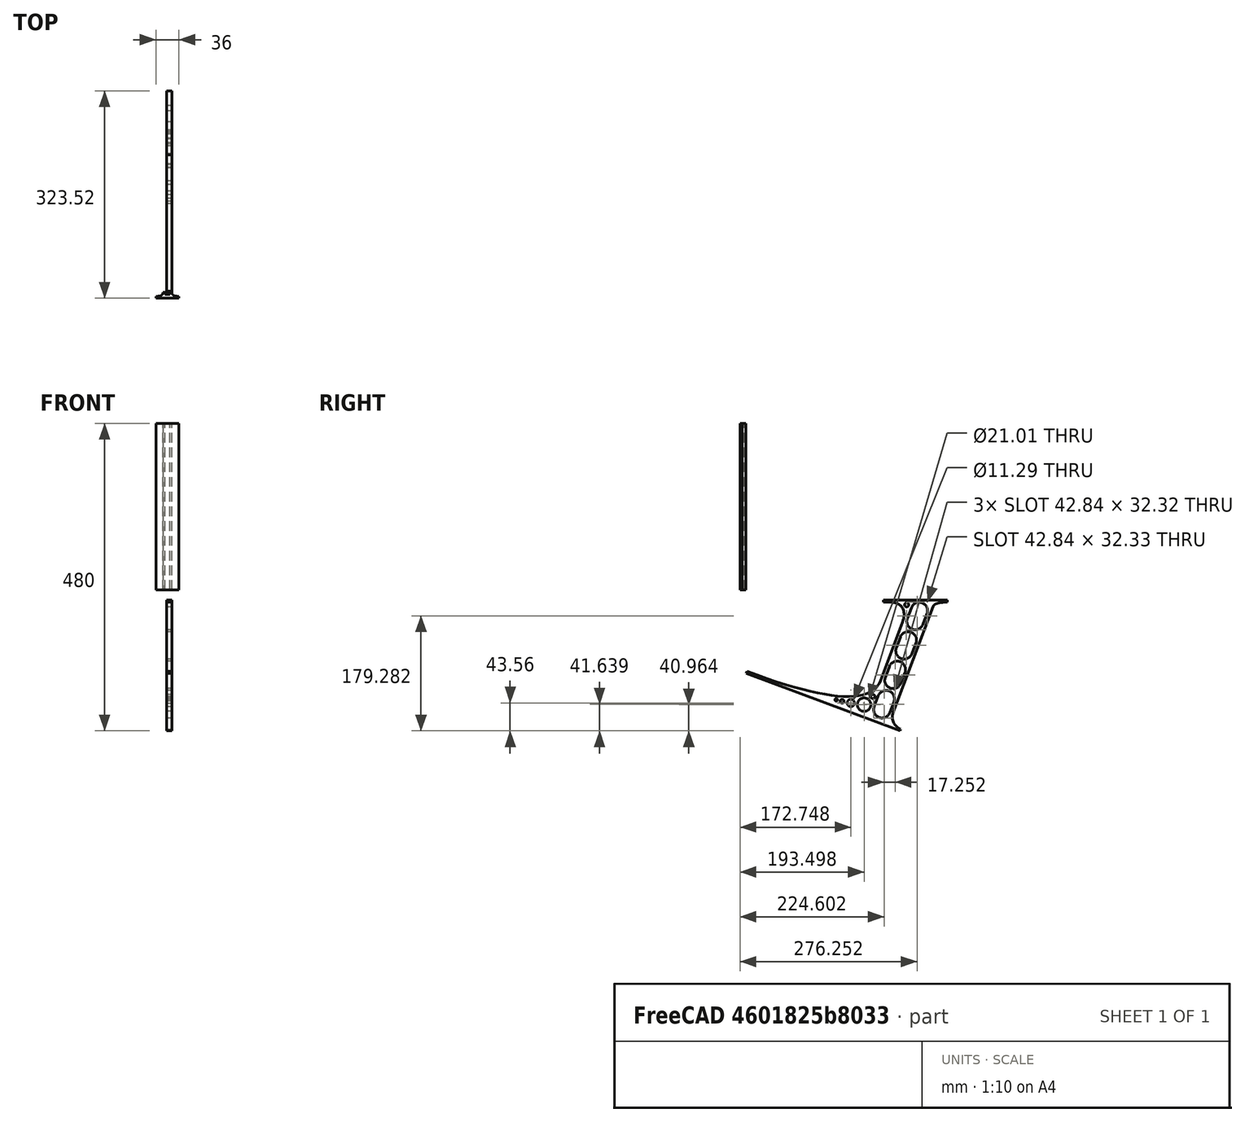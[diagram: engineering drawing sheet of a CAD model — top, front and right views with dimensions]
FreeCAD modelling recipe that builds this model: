
FCSTD DOCUMENT  (FreeCAD 0.19R0.19.2)
Label: laptopStand117FCStd
License: All rights reserved
LicenseURL: http://en.wikipedia.org/wiki/All_rights_reserved
objects: Sketcher::SketchObject×3, Part::Extrusion×3
note: 6 computed .brp shape members not serialized (recipe doc carries the construction recipe); baked Part::Feature solids carry a one-line shape summary decoded from their .brp

FEATURE [Sketcher::SketchObject] Sketch
  FullyConstrained = false
  sketch-geometry (330):
    g0: LineSegment StartX=-10.9272 StartY=-82.7794 StartZ=0 EndX=46.0728 EndY=-51.4823 EndZ=0
    g1: LineSegment StartX=-10.9272 StartY=77.3346 StartZ=0 EndX=-10.9272 EndY=-82.7794 EndZ=0
    g2: LineSegment StartX=-1.92719 StartY=-91.7794 StartZ=0 EndX=46.0728 EndY=-91.7794 EndZ=0
    g3: LineSegment StartX=46.0728 StartY=-65.424 StartZ=0 EndX=-1.92719 EndY=-91.7794 EndZ=0
    g4: LineSegment StartX=46.0728 StartY=-65.424 StartZ=0 EndX=46.0728 EndY=-91.7794 EndZ=0
    g5: LineSegment StartX=46.0728 StartY=77.3346 StartZ=0 EndX=46.0728 EndY=-51.4823 EndZ=0
    g6: LineSegment StartX=-42.9272 StartY=136.221 StartZ=0 EndX=-42.9272 EndY=-103.779 EndZ=0
    g7: LineSegment StartX=407.073 StartY=136.221 StartZ=0 EndX=407.073 EndY=-103.779 EndZ=0
    g8: ArcOfCircle CenterX=-26.9272 CenterY=22.1087 CenterZ=0 NormalX=0 NormalY=0 NormalZ=1 AngleXU=0 Radius=8 StartAngle=1e-16 EndAngle=3.14159
    g9: ArcOfCircle CenterX=-26.9272 CenterY=-83.7794 CenterZ=0 NormalX=0 NormalY=0 NormalZ=1 AngleXU=0 Radius=8 StartAngle=3.14159 EndAngle=6.28319
    g10: LineSegment StartX=-34.9272 StartY=22.1087 StartZ=0 EndX=-34.9272 EndY=-83.7794 EndZ=0
    g11: LineSegment StartX=-18.9272 StartY=22.1087 StartZ=0 EndX=-18.9272 EndY=-83.7794 EndZ=0
    g12: ArcOfCircle CenterX=391.073 CenterY=22.1087 CenterZ=0 NormalX=0 NormalY=0 NormalZ=1 AngleXU=0 Radius=8 StartAngle=-4.4e-15 EndAngle=3.14159
    g13: LineSegment StartX=399.073 StartY=22.1087 StartZ=0 EndX=399.073 EndY=-83.7794 EndZ=0
    g14: LineSegment StartX=383.073 StartY=22.1087 StartZ=0 EndX=383.073 EndY=-83.7794 EndZ=0
    g15: ArcOfCircle CenterX=391.073 CenterY=-83.7794 CenterZ=0 NormalX=0 NormalY=0 NormalZ=1 AngleXU=0 Radius=8 StartAngle=3.14159 EndAngle=6.28319
    g16: Circle CenterX=175.022 CenterY=27.0628 CenterZ=0 NormalX=0 NormalY=0 NormalZ=1 AngleXU=0 Radius=1
    g17: Circle CenterX=179.022 CenterY=24.8665 CenterZ=0 NormalX=0 NormalY=0 NormalZ=1 AngleXU=0 Radius=1
    g18: Circle CenterX=179.022 CenterY=27.0628 CenterZ=0 NormalX=0 NormalY=0 NormalZ=1 AngleXU=0 Radius=1
    g19: BSplineCurve PolesCount=3 KnotsCount=2 Degree=2 IsPeriodic=0
    g20: GeomPoint X=175.022 Y=27.0628 Z=0
    g21: GeomPoint X=179.022 Y=27.0628 Z=0
    g22: Circle CenterX=189.124 CenterY=27.0628 CenterZ=0 NormalX=0 NormalY=0 NormalZ=1 AngleXU=0 Radius=1
    g23: Circle CenterX=185.124 CenterY=24.8665 CenterZ=0 NormalX=0 NormalY=0 NormalZ=1 AngleXU=0 Radius=1
    g24: Circle CenterX=185.124 CenterY=27.0628 CenterZ=0 NormalX=0 NormalY=0 NormalZ=1 AngleXU=0 Radius=1
    g25: BSplineCurve PolesCount=3 KnotsCount=2 Degree=2 IsPeriodic=0
    g26: GeomPoint X=189.124 Y=27.0628 Z=0
    g27: GeomPoint X=185.124 Y=27.0628 Z=0
    g28: Circle CenterX=175.022 CenterY=5.37834 CenterZ=0 NormalX=0 NormalY=0 NormalZ=1 AngleXU=0 Radius=1
    g29: Circle CenterX=179.022 CenterY=7.57463 CenterZ=0 NormalX=0 NormalY=0 NormalZ=1 AngleXU=0 Radius=1
    g30: Circle CenterX=179.022 CenterY=5.34704 CenterZ=0 NormalX=0 NormalY=0 NormalZ=1 AngleXU=0 Radius=1
    g31: BSplineCurve PolesCount=3 KnotsCount=2 Degree=2 IsPeriodic=0
    g32: GeomPoint X=175.022 Y=5.37834 Z=0
    g33: GeomPoint X=179.022 Y=5.34704 Z=0
    g34: Circle CenterX=189.124 CenterY=5.37834 CenterZ=0 NormalX=0 NormalY=0 NormalZ=1 AngleXU=0 Radius=1
    g35: Circle CenterX=185.124 CenterY=7.57463 CenterZ=0 NormalX=0 NormalY=0 NormalZ=1 AngleXU=0 Radius=1
    g36: Circle CenterX=185.124 CenterY=5.34704 CenterZ=0 NormalX=0 NormalY=0 NormalZ=1 AngleXU=0 Radius=1
    g37: BSplineCurve PolesCount=3 KnotsCount=2 Degree=2 IsPeriodic=0
    g38: GeomPoint X=189.124 Y=5.37834 Z=0
    g39: GeomPoint X=185.124 Y=5.34704 Z=0
    g40: Circle CenterX=165.871 CenterY=18.1458 CenterZ=0 NormalX=0 NormalY=0 NormalZ=1 AngleXU=0 Radius=1
    g41: Circle CenterX=169.377 CenterY=16.2206 CenterZ=0 NormalX=0 NormalY=0 NormalZ=1 AngleXU=0 Radius=1
    g42: Circle CenterX=165.871 CenterY=14.2954 CenterZ=0 NormalX=0 NormalY=0 NormalZ=1 AngleXU=0 Radius=1
    g43: BSplineCurve PolesCount=3 KnotsCount=2 Degree=2 IsPeriodic=0
    g44: GeomPoint X=165.871 Y=18.1458 Z=0
    g45: GeomPoint X=165.871 Y=14.2954 Z=0
    g46: Circle CenterX=198.275 CenterY=18.1458 CenterZ=0 NormalX=0 NormalY=0 NormalZ=1 AngleXU=0 Radius=1
    g47: Circle CenterX=194.768 CenterY=16.2206 CenterZ=0 NormalX=0 NormalY=0 NormalZ=1 AngleXU=0 Radius=1
    g48: Circle CenterX=198.275 CenterY=14.2954 CenterZ=0 NormalX=0 NormalY=0 NormalZ=1 AngleXU=0 Radius=1
    g49: BSplineCurve PolesCount=3 KnotsCount=2 Degree=2 IsPeriodic=0
    g50: GeomPoint X=198.275 Y=18.1458 Z=0
    g51: GeomPoint X=198.275 Y=14.2954 Z=0
    g52: LineSegment StartX=407.073 StartY=-103.779 StartZ=0 EndX=-42.9272 EndY=-103.779 EndZ=0
    g53: LineSegment StartX=407.073 StartY=136.221 StartZ=0 EndX=-42.9272 EndY=136.221 EndZ=0
    g54: LineSegment StartX=46.0728 StartY=77.3346 StartZ=0 EndX=-10.9272 EndY=77.3346 EndZ=0
    g55: Circle CenterX=125.607 CenterY=54.1951 CenterZ=0 NormalX=0 NormalY=0 NormalZ=1 AngleXU=0 Radius=1
    g56: Circle CenterX=139.632 CenterY=46.4944 CenterZ=0 NormalX=0 NormalY=0 NormalZ=1 AngleXU=0 Radius=1
    g57: Circle CenterX=127.326 CenterY=56.7187 CenterZ=0 NormalX=0 NormalY=0 NormalZ=1 AngleXU=0 Radius=1
    g58: BSplineCurve PolesCount=3 KnotsCount=2 Degree=2 IsPeriodic=0
    g59: GeomPoint X=125.607 Y=54.1951 Z=0
    g60: GeomPoint X=127.326 Y=56.7187 Z=0
    g61: Circle CenterX=236.821 CenterY=56.7187 CenterZ=0 NormalX=0 NormalY=0 NormalZ=1 AngleXU=0 Radius=1
    g62: Circle CenterX=224.513 CenterY=46.4944 CenterZ=0 NormalX=0 NormalY=0 NormalZ=1 AngleXU=0 Radius=1
    g63: Circle CenterX=238.538 CenterY=54.1951 CenterZ=0 NormalX=0 NormalY=0 NormalZ=1 AngleXU=0 Radius=1
    g64: BSplineCurve PolesCount=3 KnotsCount=2 Degree=2 IsPeriodic=0
    g65: GeomPoint X=236.821 Y=56.7187 Z=0
    g66: GeomPoint X=238.538 Y=54.1951 Z=0
    g67: Circle CenterX=238.538 CenterY=-21.7539 CenterZ=0 NormalX=0 NormalY=0 NormalZ=1 AngleXU=0 Radius=1
    g68: Circle CenterX=224.513 CenterY=-14.0532 CenterZ=0 NormalX=0 NormalY=0 NormalZ=1 AngleXU=0 Radius=1
    g69: Circle CenterX=236.821 CenterY=-24.2775 CenterZ=0 NormalX=0 NormalY=0 NormalZ=1 AngleXU=0 Radius=1
    g70: BSplineCurve PolesCount=3 KnotsCount=2 Degree=2 IsPeriodic=0
    g71: GeomPoint X=238.538 Y=-21.7539 Z=0
    g72: GeomPoint X=236.821 Y=-24.2775 Z=0
    g73: Circle CenterX=125.607 CenterY=-21.7539 CenterZ=0 NormalX=0 NormalY=0 NormalZ=1 AngleXU=0 Radius=1
    g74: Circle CenterX=139.632 CenterY=-14.0532 CenterZ=0 NormalX=0 NormalY=0 NormalZ=1 AngleXU=0 Radius=1
    g75: Circle CenterX=127.325 CenterY=-24.2775 CenterZ=0 NormalX=0 NormalY=0 NormalZ=1 AngleXU=0 Radius=1
    g76: BSplineCurve PolesCount=3 KnotsCount=2 Degree=2 IsPeriodic=0
    g77: GeomPoint X=125.607 Y=-21.7539 Z=0
    g78: GeomPoint X=127.325 Y=-24.2775 Z=0
    g79: Circle CenterX=302.996 CenterY=111.695 CenterZ=0 NormalX=0 NormalY=0 NormalZ=1 AngleXU=0 Radius=1
    g80: Circle CenterX=306.073 CenterY=114.251 CenterZ=0 NormalX=0 NormalY=0 NormalZ=1 AngleXU=0 Radius=1
    g81: Circle CenterX=306.073 CenterY=110.251 CenterZ=0 NormalX=0 NormalY=0 NormalZ=1 AngleXU=0 Radius=1
    g82: BSplineCurve PolesCount=3 KnotsCount=2 Degree=2 IsPeriodic=0
    g83: GeomPoint X=302.996 Y=111.695 Z=0
    g84: GeomPoint X=306.073 Y=110.251 Z=0
    g85: Circle CenterX=306.073 CenterY=95.2763 CenterZ=0 NormalX=0 NormalY=0 NormalZ=1 AngleXU=0 Radius=1
    g86: Circle CenterX=306.073 CenterY=91.2763 CenterZ=0 NormalX=0 NormalY=0 NormalZ=1 AngleXU=0 Radius=1
    g87: Circle CenterX=302.567 CenterY=89.3511 CenterZ=0 NormalX=0 NormalY=0 NormalZ=1 AngleXU=0 Radius=1
    g88: BSplineCurve PolesCount=3 KnotsCount=2 Degree=2 IsPeriodic=0
    g89: GeomPoint X=306.073 Y=95.2763 Z=0
    g90: GeomPoint X=302.567 Y=89.3511 Z=0
    g91: LineSegment StartX=306.073 StartY=110.251 StartZ=0 EndX=306.073 EndY=95.2763 EndZ=0
    g92: LineSegment StartX=302.996 StartY=111.695 StartZ=0 EndX=236.821 EndY=56.7187 EndZ=0
    g93: LineSegment StartX=238.538 StartY=54.1951 StartZ=0 EndX=302.567 EndY=89.3511 EndZ=0
    g94: Circle CenterX=61.1496 CenterY=111.695 CenterZ=0 NormalX=0 NormalY=0 NormalZ=1 AngleXU=0 Radius=1
    g95: Circle CenterX=58.0728 CenterY=114.251 CenterZ=0 NormalX=0 NormalY=0 NormalZ=1 AngleXU=0 Radius=1
    g96: Circle CenterX=58.0728 CenterY=110.251 CenterZ=0 NormalX=0 NormalY=0 NormalZ=1 AngleXU=0 Radius=1
    g97: BSplineCurve PolesCount=3 KnotsCount=2 Degree=2 IsPeriodic=0
    g98: GeomPoint X=61.1496 Y=111.695 Z=0
    g99: GeomPoint X=58.0728 Y=110.251 Z=0
    g100: Circle CenterX=61.5791 CenterY=89.3511 CenterZ=0 NormalX=0 NormalY=0 NormalZ=1 AngleXU=0 Radius=1
    g101: Circle CenterX=58.0728 CenterY=91.2763 CenterZ=0 NormalX=0 NormalY=0 NormalZ=1 AngleXU=0 Radius=1
    g102: Circle CenterX=58.0728 CenterY=95.2763 CenterZ=0 NormalX=0 NormalY=0 NormalZ=1 AngleXU=0 Radius=1
    g103: BSplineCurve PolesCount=3 KnotsCount=2 Degree=2 IsPeriodic=0
    g104: GeomPoint X=61.5791 Y=89.3511 Z=0
    g105: GeomPoint X=58.0728 Y=95.2763 Z=0
    g106: LineSegment StartX=58.0728 StartY=110.251 StartZ=0 EndX=58.0728 EndY=95.2763 EndZ=0
    g107: LineSegment StartX=61.1496 StartY=111.695 StartZ=0 EndX=127.326 EndY=56.7187 EndZ=0
    g108: LineSegment StartX=125.607 StartY=54.1951 StartZ=0 EndX=61.5791 EndY=89.3511 EndZ=0
    g109: Circle CenterX=61.5791 CenterY=-56.9099 CenterZ=0 NormalX=0 NormalY=0 NormalZ=1 AngleXU=0 Radius=1
    g110: Circle CenterX=58.0728 CenterY=-58.8351 CenterZ=0 NormalX=0 NormalY=0 NormalZ=1 AngleXU=0 Radius=1
    g111: Circle CenterX=58.0728 CenterY=-62.8351 CenterZ=0 NormalX=0 NormalY=0 NormalZ=1 AngleXU=0 Radius=1
    g112: BSplineCurve PolesCount=3 KnotsCount=2 Degree=2 IsPeriodic=0
    g113: GeomPoint X=61.5791 Y=-56.9099 Z=0
    g114: GeomPoint X=58.0728 Y=-62.8351 Z=0
    g115: Circle CenterX=58.0728 CenterY=-77.8102 CenterZ=0 NormalX=0 NormalY=0 NormalZ=1 AngleXU=0 Radius=1
    g116: Circle CenterX=58.0728 CenterY=-81.8102 CenterZ=0 NormalX=0 NormalY=0 NormalZ=1 AngleXU=0 Radius=1
    g117: Circle CenterX=61.1496 CenterY=-79.2541 CenterZ=0 NormalX=0 NormalY=0 NormalZ=1 AngleXU=0 Radius=1
    g118: BSplineCurve PolesCount=3 KnotsCount=2 Degree=2 IsPeriodic=0
    g119: GeomPoint X=58.0728 Y=-77.8102 Z=0
    g120: GeomPoint X=61.1496 Y=-79.2541 Z=0
    g121: LineSegment StartX=58.0728 StartY=-62.8351 StartZ=0 EndX=58.0728 EndY=-77.8102 EndZ=0
    g122: LineSegment StartX=61.1496 StartY=-79.2541 StartZ=0 EndX=127.325 EndY=-24.2775 EndZ=0
    g123: LineSegment StartX=125.607 StartY=-21.7539 StartZ=0 EndX=61.5791 EndY=-56.9099 EndZ=0
    g124: Circle CenterX=302.567 CenterY=-56.9099 CenterZ=0 NormalX=0 NormalY=0 NormalZ=1 AngleXU=0 Radius=1
    g125: Circle CenterX=306.073 CenterY=-58.8351 CenterZ=0 NormalX=0 NormalY=0 NormalZ=1 AngleXU=0 Radius=1
    g126: Circle CenterX=306.073 CenterY=-62.8351 CenterZ=0 NormalX=0 NormalY=0 NormalZ=1 AngleXU=0 Radius=1
    g127: BSplineCurve PolesCount=3 KnotsCount=2 Degree=2 IsPeriodic=0
    g128: GeomPoint X=302.567 Y=-56.9099 Z=0
    g129: GeomPoint X=306.073 Y=-62.8351 Z=0
    g130: Circle CenterX=302.996 CenterY=-79.2541 CenterZ=0 NormalX=0 NormalY=0 NormalZ=1 AngleXU=0 Radius=1
    g131: Circle CenterX=306.073 CenterY=-81.8102 CenterZ=0 NormalX=0 NormalY=0 NormalZ=1 AngleXU=0 Radius=1
    g132: Circle CenterX=306.073 CenterY=-77.8102 CenterZ=0 NormalX=0 NormalY=0 NormalZ=1 AngleXU=0 Radius=1
    g133: BSplineCurve PolesCount=3 KnotsCount=2 Degree=2 IsPeriodic=0
    g134: GeomPoint X=302.996 Y=-79.2541 Z=0
    g135: GeomPoint X=306.073 Y=-77.8102 Z=0
    g136: LineSegment StartX=306.073 StartY=-62.8351 StartZ=0 EndX=306.073 EndY=-77.8102 EndZ=0
    g137: LineSegment StartX=302.996 StartY=-79.2541 StartZ=0 EndX=236.821 EndY=-24.2775 EndZ=0
    g138: LineSegment StartX=238.538 StartY=-21.7539 StartZ=0 EndX=302.567 EndY=-56.9099 EndZ=0
    g139: Circle CenterX=61.6457 CenterY=-88.8112 CenterZ=0 NormalX=0 NormalY=0 NormalZ=1 AngleXU=0 Radius=1
    g140: Circle CenterX=58.0728 CenterY=-91.7794 CenterZ=0 NormalX=0 NormalY=0 NormalZ=1 AngleXU=0 Radius=1
    g141: Circle CenterX=63.9135 CenterY=-91.7794 CenterZ=0 NormalX=0 NormalY=0 NormalZ=1 AngleXU=0 Radius=1
    g142: BSplineCurve PolesCount=3 KnotsCount=2 Degree=2 IsPeriodic=0
    g143: GeomPoint X=61.6457 Y=-88.8112 Z=0
    g144: GeomPoint X=63.9135 Y=-91.7794 Z=0
    g145: Circle CenterX=179.022 CenterY=-85.8163 CenterZ=0 NormalX=0 NormalY=0 NormalZ=1 AngleXU=0 Radius=1
    g146: Circle CenterX=179.022 CenterY=-91.7794 CenterZ=0 NormalX=0 NormalY=0 NormalZ=1 AngleXU=0 Radius=1
    g147: Circle CenterX=171.895 CenterY=-91.7794 CenterZ=0 NormalX=0 NormalY=0 NormalZ=1 AngleXU=0 Radius=1
    g148: BSplineCurve PolesCount=3 KnotsCount=2 Degree=2 IsPeriodic=0
    g149: GeomPoint X=179.022 Y=-85.8163 Z=0
    g150: GeomPoint X=171.895 Y=-91.7794 Z=0
    g151: Circle CenterX=185.124 CenterY=-86.2028 CenterZ=0 NormalX=0 NormalY=0 NormalZ=1 AngleXU=0 Radius=1
    g152: Circle CenterX=185.124 CenterY=-91.7794 CenterZ=0 NormalX=0 NormalY=0 NormalZ=1 AngleXU=0 Radius=1
    g153: Circle CenterX=191.747 CenterY=-91.7794 CenterZ=0 NormalX=0 NormalY=0 NormalZ=1 AngleXU=0 Radius=1
    g154: BSplineCurve PolesCount=3 KnotsCount=2 Degree=2 IsPeriodic=0
    g155: GeomPoint X=185.124 Y=-86.2028 Z=0
    g156: GeomPoint X=191.747 Y=-91.7794 Z=0
    g157: Circle CenterX=299.888 CenterY=-86.6413 CenterZ=0 NormalX=0 NormalY=0 NormalZ=1 AngleXU=0 Radius=1
    g158: Circle CenterX=306.073 CenterY=-91.7794 CenterZ=0 NormalX=0 NormalY=0 NormalZ=1 AngleXU=0 Radius=1
    g159: Circle CenterX=298.776 CenterY=-91.7794 CenterZ=0 NormalX=0 NormalY=0 NormalZ=1 AngleXU=0 Radius=1
    g160: BSplineCurve PolesCount=3 KnotsCount=2 Degree=2 IsPeriodic=0
    g161: GeomPoint X=299.888 Y=-86.6413 Z=0
    g162: GeomPoint X=298.776 Y=-91.7794 Z=0
    g163: LineSegment StartX=189.124 StartY=5.37834 StartZ=0 EndX=299.888 EndY=-86.6413 EndZ=0
    g164: LineSegment StartX=298.776 StartY=-91.7794 StartZ=0 EndX=191.747 EndY=-91.7794 EndZ=0
    g165: LineSegment StartX=185.124 StartY=-86.2028 StartZ=0 EndX=185.124 EndY=5.34704 EndZ=0
    g166: LineSegment StartX=179.022 StartY=5.34704 StartZ=0 EndX=179.022 EndY=-85.8163 EndZ=0
    g167: LineSegment StartX=171.895 StartY=-91.7794 StartZ=0 EndX=63.9135 EndY=-91.7794 EndZ=0
    g168: LineSegment StartX=61.6457 StartY=-88.8112 StartZ=0 EndX=175.022 EndY=5.37834 EndZ=0
    g169: Circle CenterX=302.073 CenterY=124.221 CenterZ=0 NormalX=0 NormalY=0 NormalZ=1 AngleXU=0 Radius=1
    g170: Circle CenterX=306.073 CenterY=124.221 CenterZ=0 NormalX=0 NormalY=0 NormalZ=1 AngleXU=0 Radius=1
    g171: Circle CenterX=302.996 CenterY=121.665 CenterZ=0 NormalX=0 NormalY=0 NormalZ=1 AngleXU=0 Radius=1
    g172: BSplineCurve PolesCount=3 KnotsCount=2 Degree=2 IsPeriodic=0
    g173: GeomPoint X=302.073 Y=124.221 Z=0
    g174: GeomPoint X=302.996 Y=121.665 Z=0
    g175: Circle CenterX=189.124 CenterY=124.221 CenterZ=0 NormalX=0 NormalY=0 NormalZ=1 AngleXU=0 Radius=1
    g176: Circle CenterX=185.124 CenterY=124.221 CenterZ=0 NormalX=0 NormalY=0 NormalZ=1 AngleXU=0 Radius=1
    g177: Circle CenterX=185.124 CenterY=120.221 CenterZ=0 NormalX=0 NormalY=0 NormalZ=1 AngleXU=0 Radius=1
    g178: BSplineCurve PolesCount=3 KnotsCount=2 Degree=2 IsPeriodic=0
    g179: GeomPoint X=189.124 Y=124.221 Z=0
    g180: GeomPoint X=185.124 Y=120.221 Z=0
    g181: Circle CenterX=175.022 CenterY=124.221 CenterZ=0 NormalX=0 NormalY=0 NormalZ=1 AngleXU=0 Radius=1
    g182: Circle CenterX=179.022 CenterY=124.221 CenterZ=0 NormalX=0 NormalY=0 NormalZ=1 AngleXU=0 Radius=1
    g183: Circle CenterX=179.022 CenterY=120.221 CenterZ=0 NormalX=0 NormalY=0 NormalZ=1 AngleXU=0 Radius=1
    g184: BSplineCurve PolesCount=3 KnotsCount=2 Degree=2 IsPeriodic=0
    g185: GeomPoint X=175.022 Y=124.221 Z=0
    g186: GeomPoint X=179.022 Y=120.221 Z=0
    g187: Circle CenterX=62.0728 CenterY=124.221 CenterZ=0 NormalX=0 NormalY=0 NormalZ=1 AngleXU=0 Radius=1
    g188: Circle CenterX=58.0728 CenterY=124.221 CenterZ=0 NormalX=0 NormalY=0 NormalZ=1 AngleXU=0 Radius=1
    g189: Circle CenterX=61.1496 CenterY=121.665 CenterZ=0 NormalX=0 NormalY=0 NormalZ=1 AngleXU=0 Radius=1
    g190: BSplineCurve PolesCount=3 KnotsCount=2 Degree=2 IsPeriodic=0
    g191: GeomPoint X=62.0728 Y=124.221 Z=0
    g192: GeomPoint X=61.1496 Y=121.665 Z=0
    g193: LineSegment StartX=62.0728 StartY=124.221 StartZ=0 EndX=175.022 EndY=124.221 EndZ=0
    g194: LineSegment StartX=179.022 StartY=120.221 StartZ=0 EndX=179.022 EndY=27.0628 EndZ=0
    g195: LineSegment StartX=185.124 StartY=27.0628 StartZ=0 EndX=185.124 EndY=120.221 EndZ=0
    g196: LineSegment StartX=189.124 StartY=124.221 StartZ=0 EndX=302.073 EndY=124.221 EndZ=0
    g197: LineSegment StartX=302.996 StartY=121.665 StartZ=0 EndX=189.124 EndY=27.0628 EndZ=0
    g198: LineSegment StartX=175.022 StartY=27.0628 StartZ=0 EndX=61.1496 EndY=121.665 EndZ=0
    g199: Circle CenterX=61.5791 CenterY=75.4095 CenterZ=0 NormalX=0 NormalY=0 NormalZ=1 AngleXU=0 Radius=1
    g200: Circle CenterX=58.0728 CenterY=77.3346 CenterZ=0 NormalX=0 NormalY=0 NormalZ=1 AngleXU=0 Radius=1
    g201: Circle CenterX=58.0728 CenterY=73.3346 CenterZ=0 NormalX=0 NormalY=0 NormalZ=1 AngleXU=0 Radius=1
    g202: BSplineCurve PolesCount=3 KnotsCount=2 Degree=2 IsPeriodic=0
    g203: GeomPoint X=61.5791 Y=75.4095 Z=0
    g204: GeomPoint X=58.0728 Y=73.3346 Z=0
    g205: Circle CenterX=58.0728 CenterY=-40.8935 CenterZ=0 NormalX=0 NormalY=0 NormalZ=1 AngleXU=0 Radius=1
    g206: Circle CenterX=58.0728 CenterY=-44.8935 CenterZ=0 NormalX=0 NormalY=0 NormalZ=1 AngleXU=0 Radius=1
    g207: Circle CenterX=61.5791 CenterY=-42.9683 CenterZ=0 NormalX=0 NormalY=0 NormalZ=1 AngleXU=0 Radius=1
    g208: BSplineCurve PolesCount=3 KnotsCount=2 Degree=2 IsPeriodic=0
    g209: GeomPoint X=58.0728 Y=-40.8935 Z=0
    g210: GeomPoint X=61.5791 Y=-42.9683 Z=0
    g211: LineSegment StartX=61.5791 StartY=-42.9683 StartZ=0 EndX=165.871 EndY=14.2954 EndZ=0
    g212: LineSegment StartX=165.871 StartY=18.1458 StartZ=0 EndX=61.5791 EndY=75.4095 EndZ=0
    g213: LineSegment StartX=58.0728 StartY=73.3346 StartZ=0 EndX=58.0728 EndY=-40.8935 EndZ=0
    g214: Circle CenterX=302.567 CenterY=-42.9683 CenterZ=0 NormalX=0 NormalY=0 NormalZ=1 AngleXU=0 Radius=1
    g215: Circle CenterX=306.073 CenterY=-44.8935 CenterZ=0 NormalX=0 NormalY=0 NormalZ=1 AngleXU=0 Radius=1
    g216: Circle CenterX=306.073 CenterY=-40.8935 CenterZ=0 NormalX=0 NormalY=0 NormalZ=1 AngleXU=0 Radius=1
    g217: BSplineCurve PolesCount=3 KnotsCount=2 Degree=2 IsPeriodic=0
    g218: GeomPoint X=302.567 Y=-42.9683 Z=0
    g219: GeomPoint X=306.073 Y=-40.8935 Z=0
    g220: Circle CenterX=306.073 CenterY=73.3346 CenterZ=0 NormalX=0 NormalY=0 NormalZ=1 AngleXU=0 Radius=1
    g221: Circle CenterX=306.073 CenterY=77.3346 CenterZ=0 NormalX=0 NormalY=0 NormalZ=1 AngleXU=0 Radius=1
    g222: Circle CenterX=302.567 CenterY=75.4095 CenterZ=0 NormalX=0 NormalY=0 NormalZ=1 AngleXU=0 Radius=1
    g223: BSplineCurve PolesCount=3 KnotsCount=2 Degree=2 IsPeriodic=0
    g224: GeomPoint X=306.073 Y=73.3346 Z=0
    g225: GeomPoint X=302.567 Y=75.4095 Z=0
    g226: LineSegment StartX=302.567 StartY=-42.9683 StartZ=0 EndX=198.275 EndY=14.2954 EndZ=0
    g227: LineSegment StartX=198.275 StartY=18.1458 StartZ=0 EndX=302.567 EndY=75.4095 EndZ=0
    g228: LineSegment StartX=306.073 StartY=73.3346 StartZ=0 EndX=306.073 EndY=-40.8935 EndZ=0
    g229: LineSegment StartX=322.073 StartY=105.865 StartZ=0 EndX=328.643 EndY=105.865 EndZ=0
    g230: LineSegment StartX=318.073 StartY=120.221 StartZ=0 EndX=318.073 EndY=109.865 EndZ=0
    g231: LineSegment StartX=336.157 StartY=107.779 StartZ=0 EndX=362.567 EndY=122.294 EndZ=0
    g232: Circle CenterX=362.073 CenterY=124.221 CenterZ=0 NormalX=0 NormalY=0 NormalZ=1 AngleXU=0 Radius=1
    g233: Circle CenterX=366.073 CenterY=124.221 CenterZ=0 NormalX=0 NormalY=0 NormalZ=1 AngleXU=0 Radius=1
    g234: Circle CenterX=362.567 CenterY=122.294 CenterZ=0 NormalX=0 NormalY=0 NormalZ=1 AngleXU=0 Radius=1
    g235: BSplineCurve PolesCount=3 KnotsCount=2 Degree=2 IsPeriodic=0
    g236: GeomPoint X=362.073 Y=124.221 Z=0
    g237: GeomPoint X=362.567 Y=122.294 Z=0
    g238: Circle CenterX=322.073 CenterY=124.221 CenterZ=0 NormalX=0 NormalY=0 NormalZ=1 AngleXU=0 Radius=1
    g239: Circle CenterX=318.073 CenterY=124.221 CenterZ=0 NormalX=0 NormalY=0 NormalZ=1 AngleXU=0 Radius=1
    g240: Circle CenterX=318.073 CenterY=120.221 CenterZ=0 NormalX=0 NormalY=0 NormalZ=1 AngleXU=0 Radius=1
    g241: BSplineCurve PolesCount=3 KnotsCount=2 Degree=2 IsPeriodic=0
    g242: GeomPoint X=322.073 Y=124.221 Z=0
    g243: GeomPoint X=318.073 Y=120.221 Z=0
    g244: Circle CenterX=322.073 CenterY=105.865 CenterZ=0 NormalX=0 NormalY=0 NormalZ=1 AngleXU=0 Radius=1
    g245: Circle CenterX=318.073 CenterY=105.865 CenterZ=0 NormalX=0 NormalY=0 NormalZ=1 AngleXU=0 Radius=1
    g246: Circle CenterX=318.073 CenterY=109.865 CenterZ=0 NormalX=0 NormalY=0 NormalZ=1 AngleXU=0 Radius=1
    g247: BSplineCurve PolesCount=3 KnotsCount=2 Degree=2 IsPeriodic=0
    g248: GeomPoint X=322.073 Y=105.865 Z=0
    g249: GeomPoint X=318.073 Y=109.865 Z=0
    g250: Circle CenterX=336.157 CenterY=107.779 CenterZ=0 NormalX=0 NormalY=0 NormalZ=1 AngleXU=0 Radius=1
    g251: Circle CenterX=332.651 CenterY=105.853 CenterZ=0 NormalX=0 NormalY=0 NormalZ=1 AngleXU=0 Radius=1
    g252: Circle CenterX=328.643 CenterY=105.865 CenterZ=0 NormalX=0 NormalY=0 NormalZ=1 AngleXU=0 Radius=1
    g253: BSplineCurve PolesCount=3 KnotsCount=2 Degree=2 IsPeriodic=0
    g254: GeomPoint X=336.157 Y=107.779 Z=0
    g255: GeomPoint X=328.643 Y=105.865 Z=0
    g256: LineSegment StartX=322.073 StartY=124.221 StartZ=0 EndX=362.073 EndY=124.221 EndZ=0
    g257: Circle CenterX=371.567 CenterY=-80.8644 CenterZ=0 NormalX=0 NormalY=0 NormalZ=1 AngleXU=0 Radius=1
    g258: Circle CenterX=375.073 CenterY=-82.7896 CenterZ=0 NormalX=0 NormalY=0 NormalZ=1 AngleXU=0 Radius=1
    g259: Circle CenterX=375.073 CenterY=-78.7896 CenterZ=0 NormalX=0 NormalY=0 NormalZ=1 AngleXU=0 Radius=1
    g260: BSplineCurve PolesCount=3 KnotsCount=2 Degree=2 IsPeriodic=0
    g261: GeomPoint X=371.567 Y=-80.8644 Z=0
    g262: GeomPoint X=375.073 Y=-78.7896 Z=0
    g263: Circle CenterX=321.579 CenterY=-53.4075 CenterZ=0 NormalX=0 NormalY=0 NormalZ=1 AngleXU=0 Radius=1
    g264: Circle CenterX=318.073 CenterY=-51.4823 CenterZ=0 NormalX=0 NormalY=0 NormalZ=1 AngleXU=0 Radius=1
    g265: Circle CenterX=318.073 CenterY=-47.4823 CenterZ=0 NormalX=0 NormalY=0 NormalZ=1 AngleXU=0 Radius=1
    g266: BSplineCurve PolesCount=3 KnotsCount=2 Degree=2 IsPeriodic=0
    g267: GeomPoint X=321.579 Y=-53.4075 Z=0
    g268: GeomPoint X=318.073 Y=-47.4823 Z=0
    g269: Circle CenterX=318.073 CenterY=79.9235 CenterZ=0 NormalX=0 NormalY=0 NormalZ=1 AngleXU=0 Radius=1
    g270: Circle CenterX=318.073 CenterY=83.9235 CenterZ=0 NormalX=0 NormalY=0 NormalZ=1 AngleXU=0 Radius=1
    g271: Circle CenterX=322.073 CenterY=83.9235 CenterZ=0 NormalX=0 NormalY=0 NormalZ=1 AngleXU=0 Radius=1
    g272: BSplineCurve PolesCount=3 KnotsCount=2 Degree=2 IsPeriodic=0
    g273: GeomPoint X=318.073 Y=79.9235 Z=0
    g274: GeomPoint X=322.073 Y=83.9235 Z=0
    g275: Circle CenterX=375.073 CenterY=79.9235 CenterZ=0 NormalX=0 NormalY=0 NormalZ=1 AngleXU=0 Radius=1
    g276: Circle CenterX=375.073 CenterY=83.9235 CenterZ=0 NormalX=0 NormalY=0 NormalZ=1 AngleXU=0 Radius=1
    g277: Circle CenterX=371.073 CenterY=83.9235 CenterZ=0 NormalX=0 NormalY=0 NormalZ=1 AngleXU=0 Radius=1
    g278: BSplineCurve PolesCount=3 KnotsCount=2 Degree=2 IsPeriodic=0
    g279: GeomPoint X=375.073 Y=79.9235 Z=0
    g280: GeomPoint X=371.073 Y=83.9235 Z=0
    g281: LineSegment StartX=322.073 StartY=83.9235 StartZ=0 EndX=371.073 EndY=83.9235 EndZ=0
    g282: LineSegment StartX=375.073 StartY=79.9235 StartZ=0 EndX=375.073 EndY=-78.7896 EndZ=0
    g283: LineSegment StartX=371.567 StartY=-80.8644 StartZ=0 EndX=321.579 EndY=-53.4075 EndZ=0
    g284: LineSegment StartX=318.073 StartY=-47.4823 StartZ=0 EndX=318.073 EndY=79.9235 EndZ=0
    g285: Circle CenterX=321.579 CenterY=-67.3492 CenterZ=0 NormalX=0 NormalY=0 NormalZ=1 AngleXU=0 Radius=1
    g286: Circle CenterX=318.073 CenterY=-65.424 CenterZ=0 NormalX=0 NormalY=0 NormalZ=1 AngleXU=0 Radius=1
    g287: Circle CenterX=318.073 CenterY=-69.424 CenterZ=0 NormalX=0 NormalY=0 NormalZ=1 AngleXU=0 Radius=1
    g288: BSplineCurve PolesCount=3 KnotsCount=2 Degree=2 IsPeriodic=0
    g289: GeomPoint X=321.579 Y=-67.3492 Z=0
    g290: GeomPoint X=318.073 Y=-69.424 Z=0
    g291: Circle CenterX=362.567 CenterY=-89.8542 CenterZ=0 NormalX=0 NormalY=0 NormalZ=1 AngleXU=0 Radius=1
    g292: Circle CenterX=366.073 CenterY=-91.7794 CenterZ=0 NormalX=0 NormalY=0 NormalZ=1 AngleXU=0 Radius=1
    g293: Circle CenterX=362.073 CenterY=-91.7794 CenterZ=0 NormalX=0 NormalY=0 NormalZ=1 AngleXU=0 Radius=1
    g294: BSplineCurve PolesCount=3 KnotsCount=2 Degree=2 IsPeriodic=0
    g295: GeomPoint X=362.567 Y=-89.8542 Z=0
    g296: GeomPoint X=362.073 Y=-91.7794 Z=0
    g297: Circle CenterX=322.073 CenterY=-91.7794 CenterZ=0 NormalX=0 NormalY=0 NormalZ=1 AngleXU=0 Radius=1
    g298: Circle CenterX=318.073 CenterY=-91.7794 CenterZ=0 NormalX=0 NormalY=0 NormalZ=1 AngleXU=0 Radius=1
    g299: Circle CenterX=318.073 CenterY=-87.7794 CenterZ=0 NormalX=0 NormalY=0 NormalZ=1 AngleXU=0 Radius=1
    g300: BSplineCurve PolesCount=3 KnotsCount=2 Degree=2 IsPeriodic=0
    g301: GeomPoint X=322.073 Y=-91.7794 Z=0
    g302: GeomPoint X=318.073 Y=-87.7794 Z=0
    g303: LineSegment StartX=362.567 StartY=-89.8542 StartZ=0 EndX=321.579 EndY=-67.3492 EndZ=0
    g304: LineSegment StartX=318.073 StartY=-69.424 StartZ=0 EndX=318.073 EndY=-87.7794 EndZ=0
    g305: LineSegment StartX=322.073 StartY=-91.7794 StartZ=0 EndX=362.073 EndY=-91.7794 EndZ=0
    g306: LineSegment StartX=46.0728 StartY=105.865 StartZ=0 EndX=42.0728 EndY=105.865 EndZ=0
    g307: Circle CenterX=2.07281 CenterY=124.221 CenterZ=0 NormalX=0 NormalY=0 NormalZ=1 AngleXU=0 Radius=1
    g308: Circle CenterX=1.57905 CenterY=122.295 CenterZ=0 NormalX=0 NormalY=0 NormalZ=1 AngleXU=0 Radius=1
    g309: BSplineCurve PolesCount=3 KnotsCount=2 Degree=2 IsPeriodic=0
    g310: GeomPoint X=2.07281 Y=124.221 Z=0
    g311: GeomPoint X=1.57905 Y=122.295 Z=0
    g312: Circle CenterX=42.0728 CenterY=124.221 CenterZ=0 NormalX=0 NormalY=0 NormalZ=1 AngleXU=0 Radius=1
    g313: Circle CenterX=46.0728 CenterY=124.221 CenterZ=0 NormalX=0 NormalY=0 NormalZ=1 AngleXU=0 Radius=1
    g314: Circle CenterX=46.0728 CenterY=120.221 CenterZ=0 NormalX=0 NormalY=0 NormalZ=1 AngleXU=0 Radius=1
    g315: BSplineCurve PolesCount=3 KnotsCount=2 Degree=2 IsPeriodic=0
    g316: GeomPoint X=42.0728 Y=124.221 Z=0
    g317: GeomPoint X=46.0728 Y=120.221 Z=0
    g318: Circle CenterX=46.0728 CenterY=109.865 CenterZ=0 NormalX=0 NormalY=0 NormalZ=1 AngleXU=0 Radius=1
    g319: Circle CenterX=46.0728 CenterY=105.865 CenterZ=0 NormalX=0 NormalY=0 NormalZ=1 AngleXU=0 Radius=1
    g320: Circle CenterX=42.0728 CenterY=105.865 CenterZ=0 NormalX=0 NormalY=0 NormalZ=1 AngleXU=0 Radius=1
    g321: BSplineCurve PolesCount=3 KnotsCount=2 Degree=2 IsPeriodic=0
    g322: GeomPoint X=46.0728 Y=109.865 Z=0
    g323: GeomPoint X=42.0728 Y=105.865 Z=0
    g324: Circle CenterX=35.5028 CenterY=105.865 CenterZ=0 NormalX=0 NormalY=0 NormalZ=1 AngleXU=0 Radius=1
    g325: Circle CenterX=31.5028 CenterY=105.865 CenterZ=0 NormalX=0 NormalY=0 NormalZ=1 AngleXU=0 Radius=1
    g326: Circle CenterX=27.9965 CenterY=107.79 CenterZ=0 NormalX=0 NormalY=0 NormalZ=1 AngleXU=0 Radius=1
    g327: BSplineCurve PolesCount=3 KnotsCount=2 Degree=2 IsPeriodic=0
    g328: GeomPoint X=35.5028 Y=105.865 Z=0
    g329: GeomPoint X=27.9965 Y=107.79 Z=0
  constraints (540):
    c: Horizontal(g2)
    c: Coincident(g4,g3)
    c: Coincident(g0,g5)
    c: Block(g4)
    c: Block(g3)
    c: Block(g0)
    c: Block(g1)
    c: Block(g2)
    c: Vertical(g6)
    c: Vertical(g7)
    c: Block(g7)
    c: Block(g6)
    c: Tangent(g8,g11) = 1.5708
    c: Tangent(g8,g10) = -1.5708
    c: Tangent(g10,g9) = -1.5708
    c: Tangent(g11,g9) = 1.5708
    c: Vertical(g10)
    c: Equal(g8,g9)
    c: Block(g11)
    c: Block(g10)
    c: Tangent(g12,g13) = 1.5708
    c: Tangent(g13,g15) = 1.5708
    c: Equal(g12,g15)
    c: Coincident(g14,g12)
    c: Coincident(g14,g15)
    c: Block(g13)
    c: Block(g14)
    c: Weight(g16) = 1
    c: Equal(g16,g17)
    c: Equal(g16,g18)
    c: InternalAlignment(g16,g19)
    c: InternalAlignment(g17,g19)
    c: InternalAlignment(g18,g19)
    c: InternalAlignment(g20,g19)
    c: InternalAlignment(g21,g19)
    c: Weight(g22) = 1
    c: Equal(g22,g23)
    c: Equal(g22,g24)
    c: InternalAlignment(g22,g25)
    c: InternalAlignment(g23,g25)
    c: InternalAlignment(g24,g25)
    c: InternalAlignment(g26,g25)
    c: InternalAlignment(g27,g25)
    c: Block(g25)
    c: Block(g19)
    c: Weight(g28) = 1
    c: Equal(g28,g29)
    c: Equal(g28,g30)
    c: InternalAlignment(g28,g31)
    c: InternalAlignment(g29,g31)
    c: InternalAlignment(g30,g31)
    c: InternalAlignment(g32,g31)
    c: InternalAlignment(g33,g31)
    c: Weight(g34) = 1
    c: Equal(g34,g35)
    c: Equal(g34,g36)
    c: InternalAlignment(g34,g37)
    c: InternalAlignment(g35,g37)
    c: InternalAlignment(g36,g37)
    c: InternalAlignment(g38,g37)
    c: InternalAlignment(g39,g37)
    c: Block(g37)
    c: Block(g31)
    c: Weight(g40) = 1
    c: Equal(g40,g41)
    c: Equal(g40,g42)
    c: InternalAlignment(g40,g43)
    c: InternalAlignment(g41,g43)
    c: InternalAlignment(g42,g43)
    c: InternalAlignment(g44,g43)
    c: InternalAlignment(g45,g43)
    c: Weight(g46) = 1
    c: Equal(g46,g47)
    c: Equal(g46,g48)
    c: InternalAlignment(g46,g49)
    c: InternalAlignment(g47,g49)
    c: InternalAlignment(g48,g49)
    c: InternalAlignment(g50,g49)
    c: InternalAlignment(g51,g49)
    c: Block(g43)
    c: Block(g49)
    c: Coincident(g52,g7)
    c: Coincident(g52,g6)
    c: Horizontal(g52)
    c: Distance(g52) = 450
    c: Coincident(g53,g7)
    c: Coincident(g53,g6)
    c: Horizontal(g53)
    c: Horizontal(g54)
    c: Coincident(g5,g54)
    c: Block(g54)
    c: Coincident(g1,g54)
    c: Weight(g55) = 1
    c: Equal(g55,g56)
    c: Equal(g55,g57)
    c: InternalAlignment(g55,g58)
    c: InternalAlignment(g56,g58)
    c: InternalAlignment(g57,g58)
    c: InternalAlignment(g59,g58)
    c: InternalAlignment(g60,g58)
    c: Block(g58)
    c: Weight(g61) = 1
    c: Equal(g61,g62)
    c: Equal(g61,g63)
    c: InternalAlignment(g61,g64)
    c: InternalAlignment(g62,g64)
    c: InternalAlignment(g63,g64)
    c: InternalAlignment(g65,g64)
    c: InternalAlignment(g66,g64)
    c: Block(g64)
    c: Weight(g67) = 1
    c: Equal(g67,g68)
    c: Equal(g67,g69)
    c: InternalAlignment(g67,g70)
    c: InternalAlignment(g68,g70)
    c: InternalAlignment(g69,g70)
    c: InternalAlignment(g71,g70)
    c: InternalAlignment(g72,g70)
    c: Block(g70)
    c: Weight(g73) = 1
    c: Equal(g73,g74)
    c: Equal(g73,g75)
    c: InternalAlignment(g73,g76)
    c: InternalAlignment(g74,g76)
    c: InternalAlignment(g75,g76)
    c: InternalAlignment(g77,g76)
    c: InternalAlignment(g78,g76)
    c: Block(g76)
    c: Weight(g79) = 1
    c: Equal(g79,g80)
    c: Equal(g79,g81)
    c: InternalAlignment(g79,g82)
    c: InternalAlignment(g80,g82)
    c: InternalAlignment(g81,g82)
    c: InternalAlignment(g83,g82)
    c: InternalAlignment(g84,g82)
    c: Weight(g85) = 1
    c: Equal(g85,g86)
    c: Equal(g85,g87)
    c: InternalAlignment(g85,g88)
    c: InternalAlignment(g86,g88)
    c: InternalAlignment(g87,g88)
    c: InternalAlignment(g89,g88)
    c: InternalAlignment(g90,g88)
    c: Block(g82)
    c: Block(g88)
    c: Coincident(g91,g82)
    c: Coincident(g91,g88)
    c: Vertical(g91)
    c: Coincident(g92,g82)
    c: Coincident(g92,g64)
    c: Coincident(g93,g64)
    c: Coincident(g93,g88)
    c: Weight(g94) = 1
    c: Equal(g94,g95)
    c: Equal(g94,g96)
    c: InternalAlignment(g94,g97)
    c: InternalAlignment(g95,g97)
    c: InternalAlignment(g96,g97)
    c: InternalAlignment(g98,g97)
    c: InternalAlignment(g99,g97)
    c: Weight(g100) = 1
    c: Equal(g100,g101)
    c: Equal(g100,g102)
    c: InternalAlignment(g100,g103)
    c: InternalAlignment(g101,g103)
    c: InternalAlignment(g102,g103)
    c: InternalAlignment(g104,g103)
    c: InternalAlignment(g105,g103)
    c: Block(g97)
    c: Block(g103)
    c: Coincident(g106,g97)
    c: Coincident(g106,g103)
    c: Vertical(g106)
    c: Coincident(g107,g97)
    c: Coincident(g107,g58)
    c: Coincident(g108,g58)
    c: Coincident(g108,g103)
    c: Weight(g109) = 1
    c: Equal(g109,g110)
    c: Equal(g109,g111)
    c: InternalAlignment(g109,g112)
    c: InternalAlignment(g110,g112)
    c: InternalAlignment(g111,g112)
    c: InternalAlignment(g113,g112)
    c: InternalAlignment(g114,g112)
    c: Weight(g115) = 1
    c: Equal(g115,g116)
    c: Equal(g115,g117)
    c: InternalAlignment(g115,g118)
    c: InternalAlignment(g116,g118)
    c: InternalAlignment(g117,g118)
    c: InternalAlignment(g119,g118)
    c: InternalAlignment(g120,g118)
    c: Block(g112)
    c: Block(g118)
    c: Coincident(g121,g112)
    c: Coincident(g121,g118)
    c: Vertical(g121)
    c: Coincident(g122,g118)
    c: Coincident(g122,g76)
    c: Coincident(g123,g76)
    c: Coincident(g123,g112)
    c: Weight(g124) = 1
    c: Equal(g124,g125)
    c: Equal(g124,g126)
    c: InternalAlignment(g124,g127)
    c: InternalAlignment(g125,g127)
    c: InternalAlignment(g126,g127)
    c: InternalAlignment(g128,g127)
    c: InternalAlignment(g129,g127)
    c: Weight(g130) = 1
    c: Equal(g130,g131)
    c: Equal(g130,g132)
    c: InternalAlignment(g130,g133)
    c: InternalAlignment(g131,g133)
    c: InternalAlignment(g132,g133)
    c: InternalAlignment(g134,g133)
    c: InternalAlignment(g135,g133)
    c: Block(g127)
    c: Block(g133)
    c: Coincident(g136,g127)
    c: Coincident(g136,g133)
    c: Vertical(g136)
    c: Coincident(g137,g133)
    c: Coincident(g137,g70)
    c: Coincident(g138,g70)
    c: Coincident(g138,g127)
    c: Weight(g139) = 1
    c: Equal(g139,g140)
    c: Equal(g139,g141)
    c: InternalAlignment(g139,g142)
    c: InternalAlignment(g140,g142)
    c: InternalAlignment(g141,g142)
    c: InternalAlignment(g143,g142)
    c: InternalAlignment(g144,g142)
    c: Weight(g145) = 1
    c: Equal(g145,g146)
    c: Equal(g145,g147)
    c: InternalAlignment(g145,g148)
    c: InternalAlignment(g146,g148)
    c: InternalAlignment(g147,g148)
    c: InternalAlignment(g149,g148)
    c: InternalAlignment(g150,g148)
    c: Weight(g151) = 1
    c: Equal(g151,g152)
    c: Equal(g151,g153)
    c: InternalAlignment(g151,g154)
    c: InternalAlignment(g152,g154)
    c: InternalAlignment(g153,g154)
    c: InternalAlignment(g155,g154)
    c: InternalAlignment(g156,g154)
    c: Weight(g157) = 1
    c: Equal(g157,g158)
    c: Equal(g157,g159)
    c: InternalAlignment(g157,g160)
    c: InternalAlignment(g158,g160)
    c: InternalAlignment(g159,g160)
    c: InternalAlignment(g161,g160)
    c: InternalAlignment(g162,g160)
    c: Block(g160)
    c: Block(g154)
    c: Block(g148)
    c: Block(g142)
    c: Coincident(g163,g37)
    c: Coincident(g163,g160)
    c: Coincident(g164,g160)
    c: Coincident(g164,g154)
    c: Horizontal(g164)
    c: Coincident(g165,g154)
    c: Coincident(g165,g37)
    c: Vertical(g165)
    c: Coincident(g166,g31)
    c: Coincident(g166,g148)
    c: Vertical(g166)
    c: Coincident(g167,g148)
    c: Coincident(g167,g142)
    c: Horizontal(g167)
    c: Coincident(g168,g142)
    c: Coincident(g168,g31)
    c: Weight(g169) = 1
    c: Equal(g169,g170)
    c: Equal(g169,g171)
    c: InternalAlignment(g169,g172)
    c: InternalAlignment(g170,g172)
    c: InternalAlignment(g171,g172)
    c: InternalAlignment(g173,g172)
    c: InternalAlignment(g174,g172)
    c: Weight(g175) = 1
    c: Equal(g175,g176)
    c: Equal(g175,g177)
    c: InternalAlignment(g175,g178)
    c: InternalAlignment(g176,g178)
    c: InternalAlignment(g177,g178)
    c: InternalAlignment(g179,g178)
    c: InternalAlignment(g180,g178)
    c: Weight(g181) = 1
    c: Equal(g181,g182)
    c: Equal(g181,g183)
    c: InternalAlignment(g181,g184)
    c: InternalAlignment(g182,g184)
    c: InternalAlignment(g183,g184)
    c: InternalAlignment(g185,g184)
    c: InternalAlignment(g186,g184)
    c: Weight(g187) = 1
    c: Equal(g187,g188)
    c: Equal(g187,g189)
    c: InternalAlignment(g187,g190)
    c: InternalAlignment(g188,g190)
    c: InternalAlignment(g189,g190)
    c: InternalAlignment(g191,g190)
    c: InternalAlignment(g192,g190)
    c: Block(g190)
    c: Block(g184)
    c: Block(g178)
    c: Block(g172)
    c: Coincident(g193,g190)
    c: Coincident(g193,g184)
    c: Horizontal(g193)
    c: Coincident(g194,g184)
    c: Coincident(g194,g19)
    c: Vertical(g194)
    c: Coincident(g195,g25)
    c: Coincident(g195,g178)
    c: Vertical(g195)
    c: Coincident(g196,g178)
    c: Coincident(g196,g172)
    c: Horizontal(g196)
    c: Coincident(g197,g172)
    c: Coincident(g197,g25)
    c: Coincident(g198,g19)
    c: Weight(g199) = 1
    c: Equal(g199,g200)
    c: Equal(g199,g201)
    c: InternalAlignment(g199,g202)
    c: InternalAlignment(g200,g202)
    c: InternalAlignment(g201,g202)
    c: InternalAlignment(g203,g202)
    c: InternalAlignment(g204,g202)
    c: Weight(g205) = 1
    c: Equal(g205,g206)
    c: Equal(g205,g207)
    c: InternalAlignment(g205,g208)
    c: InternalAlignment(g206,g208)
    c: InternalAlignment(g207,g208)
    c: InternalAlignment(g209,g208)
    c: InternalAlignment(g210,g208)
    c: Block(g208)
    c: Block(g202)
    c: Coincident(g211,g208)
    c: Coincident(g211,g43)
    c: Coincident(g212,g43)
    c: Coincident(g212,g202)
    c: Coincident(g213,g202)
    c: Coincident(g213,g208)
    c: Vertical(g213)
    c: Weight(g214) = 1
    c: Equal(g214,g215)
    c: Equal(g214,g216)
    c: InternalAlignment(g214,g217)
    c: InternalAlignment(g215,g217)
    c: InternalAlignment(g216,g217)
    c: InternalAlignment(g218,g217)
    c: InternalAlignment(g219,g217)
    c: Weight(g220) = 1
    c: Equal(g220,g221)
    c: Equal(g220,g222)
    c: InternalAlignment(g220,g223)
    c: InternalAlignment(g221,g223)
    c: InternalAlignment(g222,g223)
    c: InternalAlignment(g224,g223)
    c: InternalAlignment(g225,g223)
    c: Block(g223)
    c: Block(g217)
    c: Coincident(g226,g217)
    c: Coincident(g226,g49)
    c: Coincident(g227,g49)
    c: Coincident(g227,g223)
    c: Coincident(g228,g223)
    c: Coincident(g228,g217)
    c: Vertical(g228)
    c: Horizontal(g229)
    c: Block(g229)
    c: Vertical(g230)
    c: Block(g230)
    c: Block(g231)
    c: Weight(g232) = 1
    c: Equal(g232,g233)
    c: Equal(g232,g234)
    c: InternalAlignment(g232,g235)
    c: InternalAlignment(g233,g235)
    c: InternalAlignment(g234,g235)
    c: InternalAlignment(g236,g235)
    c: InternalAlignment(g237,g235)
    c: Weight(g238) = 1
    c: Equal(g238,g239)
    c: Equal(g238,g240)
    c: InternalAlignment(g238,g241)
    c: InternalAlignment(g239,g241)
    c: InternalAlignment(g240,g241)
    c: InternalAlignment(g242,g241)
    c: InternalAlignment(g243,g241)
    c: Weight(g244) = 1
    c: Equal(g244,g245)
    c: Equal(g244,g246)
    c: InternalAlignment(g244,g247)
    c: InternalAlignment(g245,g247)
    c: InternalAlignment(g246,g247)
    c: InternalAlignment(g248,g247)
    c: InternalAlignment(g249,g247)
    c: Weight(g250) = 1
    c: Equal(g250,g251)
    c: Equal(g250,g252)
    c: InternalAlignment(g250,g253)
    c: InternalAlignment(g251,g253)
    c: InternalAlignment(g252,g253)
    c: InternalAlignment(g254,g253)
    c: InternalAlignment(g255,g253)
    c: Block(g235)
    c: Block(g241)
    c: Block(g247)
    c: Block(g253)
    c: Coincident(g256,g241)
    c: Coincident(g256,g235)
    c: Horizontal(g256)
    c: Block(g198)
    c: Weight(g257) = 1
    c: Equal(g257,g258)
    c: Equal(g257,g259)
    c: InternalAlignment(g257,g260)
    c: InternalAlignment(g258,g260)
    c: InternalAlignment(g259,g260)
    c: InternalAlignment(g261,g260)
    c: InternalAlignment(g262,g260)
    c: Weight(g263) = 1
    c: Equal(g263,g264)
    c: Equal(g263,g265)
    c: InternalAlignment(g263,g266)
    c: InternalAlignment(g264,g266)
    c: InternalAlignment(g265,g266)
    c: InternalAlignment(g267,g266)
    c: InternalAlignment(g268,g266)
    c: Weight(g269) = 1
    c: Equal(g269,g270)
    c: Equal(g269,g271)
    c: InternalAlignment(g269,g272)
    c: InternalAlignment(g270,g272)
    c: InternalAlignment(g271,g272)
    c: InternalAlignment(g273,g272)
    c: InternalAlignment(g274,g272)
    c: Weight(g275) = 1
    c: Equal(g275,g276)
    c: Equal(g275,g277)
    c: InternalAlignment(g275,g278)
    c: InternalAlignment(g276,g278)
    c: InternalAlignment(g277,g278)
    c: InternalAlignment(g279,g278)
    c: InternalAlignment(g280,g278)
    c: Block(g260)
    c: Block(g266)
    c: Block(g272)
    c: Block(g278)
    c: Coincident(g281,g272)
    c: Coincident(g281,g278)
    c: Horizontal(g281)
    c: Coincident(g282,g278)
    c: Coincident(g282,g260)
    c: Vertical(g282)
    c: Coincident(g283,g260)
    c: Coincident(g283,g266)
    c: Coincident(g284,g266)
    c: Coincident(g284,g272)
    c: Vertical(g284)
    c: Weight(g285) = 1
    c: Equal(g285,g286)
    c: Equal(g285,g287)
    c: InternalAlignment(g285,g288)
    c: InternalAlignment(g286,g288)
    c: InternalAlignment(g287,g288)
    c: InternalAlignment(g289,g288)
    c: InternalAlignment(g290,g288)
    c: Weight(g291) = 1
    c: Equal(g291,g292)
    c: Equal(g291,g293)
    c: InternalAlignment(g291,g294)
    c: InternalAlignment(g292,g294)
    c: InternalAlignment(g293,g294)
    c: InternalAlignment(g295,g294)
    c: InternalAlignment(g296,g294)
    c: Weight(g297) = 1
    c: Equal(g297,g298)
    c: Equal(g297,g299)
    c: InternalAlignment(g297,g300)
    c: InternalAlignment(g298,g300)
    c: InternalAlignment(g299,g300)
    c: InternalAlignment(g301,g300)
    c: InternalAlignment(g302,g300)
    c: Block(g300)
    c: Block(g294)
    c: Block(g288)
    c: Coincident(g303,g294)
    c: Coincident(g303,g288)
    c: Coincident(g304,g288)
    c: Coincident(g304,g300)
    c: Vertical(g304)
    c: Coincident(g305,g300)
    c: Coincident(g305,g294)
    c: Horizontal(g305)
    c: Horizontal(g306)
    c: Distance(g306) = 4
    c: Weight(g307) = 1
    c: Equal(g307,g308)
    c: InternalAlignment(g307,g309)
    c: InternalAlignment(g308,g309)
    c: InternalAlignment(g310,g309)
    c: InternalAlignment(g311,g309)
    c: Weight(g312) = 1
    c: Equal(g312,g313)
    c: Equal(g312,g314)
    c: InternalAlignment(g312,g315)
    c: InternalAlignment(g313,g315)
    c: InternalAlignment(g314,g315)
    c: InternalAlignment(g316,g315)
    c: InternalAlignment(g317,g315)
    c: Weight(g318) = 1
    c: Equal(g318,g319)
    c: Equal(g318,g320)
    c: Coincident(g321,g306)
    c: InternalAlignment(g318,g321)
    c: InternalAlignment(g319,g321)
    c: InternalAlignment(g320,g321)
    c: InternalAlignment(g322,g321)
    c: InternalAlignment(g323,g321)
    c: Equal(g324,g325)
    c: Equal(g324,g326)
    c: InternalAlignment(g324,g327)
    c: InternalAlignment(g325,g327)
    c: InternalAlignment(g326,g327)
    c: InternalAlignment(g328,g327)
    c: InternalAlignment(g329,g327)
FEATURE [Sketcher::SketchObject] Sketch001
  FullyConstrained = true
  MapMode = 4
  Placement = pos=(0,0,0) rot=(0.57735,0.57735,0.57735;2.0944rad)
  Support = -> [Sketch]
  sketch-geometry (46):
    g0: BSplineCurve PolesCount=3 KnotsCount=2 Degree=2 IsPeriodic=0
    g1: ArcOfCircle CenterX=73.1223 CenterY=-32.291 CenterZ=0 NormalX=0 NormalY=0 NormalZ=1 AngleXU=0 Radius=13 StartAngle=5.92268 EndAngle=9.06428
    g2: ArcOfCircle CenterX=66.7816 CenterY=-49.1439 CenterZ=0 NormalX=0 NormalY=0 NormalZ=1 AngleXU=0 Radius=13 StartAngle=2.78068 EndAngle=5.92131
    g3: ArcOfCircle CenterX=55.9263 CenterY=-78.1807 CenterZ=0 NormalX=0 NormalY=0 NormalZ=1 AngleXU=0 Radius=13 StartAngle=5.92268 EndAngle=9.06428
    g4: ArcOfCircle CenterX=49.5884 CenterY=-95.0342 CenterZ=0 NormalX=0 NormalY=0 NormalZ=1 AngleXU=0 Radius=13 StartAngle=2.78068 EndAngle=5.92131
    g5: ArcOfCircle CenterX=38.7206 CenterY=-124.067 CenterZ=0 NormalX=0 NormalY=0 NormalZ=1 AngleXU=0 Radius=13 StartAngle=5.92268 EndAngle=9.06428
    g6: ArcOfCircle CenterX=32.3875 CenterY=-140.92 CenterZ=0 NormalX=0 NormalY=0 NormalZ=1 AngleXU=0 Radius=13 StartAngle=2.78068 EndAngle=5.92131
    g7: ArcOfCircle CenterX=21.4715 CenterY=-169.934 CenterZ=0 NormalX=0 NormalY=0 NormalZ=1 AngleXU=0 Radius=13 StartAngle=5.92268 EndAngle=9.06428
    g8: ArcOfCircle CenterX=15.1336 CenterY=-186.787 CenterZ=0 NormalX=0 NormalY=0 NormalZ=1 AngleXU=0 Radius=13 StartAngle=2.78068 EndAngle=5.92131
    g9-g12: Circle x4 (B-spline internal-alignment scaffolding for g13; pole/knot coordinates omitted)
    g13: BSplineCurve PolesCount=4 KnotsCount=2 Degree=3 IsPeriodic=0
    g14: GeomPoint X=28.8094 Y=-19.0875 Z=0
    g15: GeomPoint X=47.0443 Y=-50.4712 Z=0
    g16: Circle CenterX=53.5586 CenterY=-23.2695 CenterZ=0 NormalX=0 NormalY=0 NormalZ=1 AngleXU=0 Radius=3.24518
    g17: Circle CenterX=-195.441 CenterY=-127.082 CenterZ=0 NormalX=0 NormalY=0 NormalZ=1 AngleXU=0 Radius=1
    g18: Circle CenterX=-8.24091 CenterY=-197.481 CenterZ=0 NormalX=0 NormalY=0 NormalZ=1 AngleXU=0 Radius=1
    g19: Circle CenterX=12.8789 CenterY=-141.321 CenterZ=0 NormalX=0 NormalY=0 NormalZ=1 AngleXU=0 Radius=1
    g20: BSplineCurve PolesCount=3 KnotsCount=2 Degree=2 IsPeriodic=0
    g21: GeomPoint X=-195.441 Y=-127.082 Z=0
    g22: GeomPoint X=12.8789 Y=-141.321 Z=0
    g23: Circle CenterX=-12.8016 CenterY=-179.036 CenterZ=0 NormalX=0 NormalY=0 NormalZ=1 AngleXU=0 Radius=10.5072
    g24: Circle CenterX=0.933922 CenterY=-166.43 CenterZ=0 NormalX=0 NormalY=0 NormalZ=1 AngleXU=0 Radius=3.26661
    g25: Circle CenterX=-33.5518 CenterY=-176.44 CenterZ=0 NormalX=0 NormalY=0 NormalZ=1 AngleXU=0 Radius=5.64388
    g26: Circle CenterX=-47.2366 CenterY=-173.859 CenterZ=0 NormalX=0 NormalY=0 NormalZ=1 AngleXU=0 Radius=3.01653
    g27: Circle CenterX=-56.2595 CenterY=-171.456 CenterZ=0 NormalX=0 NormalY=0 NormalZ=1 AngleXU=0 Radius=2.12826
    g28: ArcOfCircle CenterX=51.2151 CenterY=-198.473 CenterZ=0 NormalX=0 NormalY=0 NormalZ=1 AngleXU=0 Radius=20 StartAngle=2.78189 EndAngle=4.35269
    g29: LineSegment StartX=32.4951 StartY=-191.433 StartZ=0 EndX=94.6578 EndY=-26.1352 EndZ=0
    g30: LineSegment StartX=43.1192 StartY=-220.001 StartZ=0 EndX=-196.497 EndY=-129.89 EndZ=0
    g31: LineSegment StartX=43.1192 StartY=-220.001 StartZ=0 EndX=44.1752 EndY=-217.193 EndZ=0
    g32: LineSegment StartX=117.223 StartY=-19.0875 StartZ=0 EndX=117.223 EndY=-16.0875 EndZ=0
    g33: LineSegment StartX=117.223 StartY=-16.0875 StartZ=0 EndX=17.2232 EndY=-16.0875 EndZ=0
    g34: LineSegment StartX=17.2232 StartY=-16.0875 StartZ=0 EndX=17.2232 EndY=-19.0875 EndZ=0
    g35: LineSegment StartX=28.8094 StartY=-19.0875 StartZ=0 EndX=17.2232 EndY=-19.0875 EndZ=0
    g36: LineSegment StartX=47.0443 StartY=-50.4712 StartZ=0 EndX=12.8789 EndY=-141.321 EndZ=0
    g37: LineSegment StartX=-195.441 StartY=-127.082 StartZ=0 EndX=-196.497 EndY=-129.89 EndZ=0
    g38: LineSegment StartX=85.2866 StartY=-36.8766 StartZ=0 EndX=78.9396 EndY=-53.7463 EndZ=0
    g39: LineSegment StartX=60.9579 StartY=-27.7053 StartZ=0 EndX=54.6191 EndY=-44.5532 EndZ=0
    g40: LineSegment StartX=68.0907 StartY=-82.7664 StartZ=0 EndX=61.7465 EndY=-99.6365 EndZ=0
    g41: LineSegment StartX=43.7619 StartY=-73.595 StartZ=0 EndX=37.426 EndY=-90.4435 EndZ=0
    g42: LineSegment StartX=50.885 StartY=-128.652 StartZ=0 EndX=44.5456 EndY=-145.522 EndZ=0
    g43: LineSegment StartX=26.5562 StartY=-119.481 StartZ=0 EndX=20.2251 EndY=-136.329 EndZ=0
    g44: LineSegment StartX=9.3071 StartY=-165.349 StartZ=0 EndX=2.97115 EndY=-182.197 EndZ=0
    g45: LineSegment StartX=33.6358 StartY=-174.52 StartZ=0 EndX=27.2917 EndY=-191.39 EndZ=0
  constraints (71):
    c: Block(g0)
    c: Block(g1)
    c: Block(g2)
    c: Block(g4)
    c: Block(g3)
    c: Block(g6)
    c: Block(g5)
    c: Block(g8)
    c: Block(g7)
    c: Weight(g9) = 1
    c: Equal(g9,g10)
    c: Equal(g9,g11)
    c: Equal(g9,g12)
    c: InternalAlignment(g9-g12 -> g13) x4
    c: InternalAlignment(g14,g13)
    c: InternalAlignment(g15,g13)
    c: Block(g16)
    c: Weight(g17) = 1
    c: Equal(g17,g18)
    c: Equal(g17,g19)
    c: InternalAlignment(g17,g20)
    c: InternalAlignment(g18,g20)
    c: InternalAlignment(g19,g20)
    c: InternalAlignment(g21,g20)
    c: InternalAlignment(g22,g20)
    c: Block(g20)
    c: Block(g23)
    c: Block(g24)
    c: Block(g25)
    c: Block(g26)
    c: Block(g27)
    c: Block(g28)
    c: Coincident(g29,g28)
    c: Coincident(g29,g0)
    c: Block(g13)
    c: Coincident(g31,g30)
    c: Coincident(g31,g28)
    c: Block(g31)
    c: Coincident(g32,g0)
    c: Vertical(g32)
    c: Coincident(g33,g32)
    c: Horizontal(g33)
    c: Coincident(g34,g33)
    c: Vertical(g34)
    c: Block(g33)
    c: Coincident(g35,g13)
    c: Coincident(g35,g34)
    c: Horizontal(g35)
    c: Coincident(g36,g13)
    c: Coincident(g36,g20)
    c: Coincident(g37,g20)
    c: Coincident(g37,g30)
    c: Block(g30)
    c: Coincident(g38,g1)
    c: Coincident(g38,g2)
    c: Coincident(g39,g1)
    c: Coincident(g39,g2)
    c: Coincident(g40,g3)
    c: Coincident(g40,g4)
    c: Coincident(g41,g3)
    c: Coincident(g41,g4)
    c: Coincident(g42,g5)
    c: Coincident(g42,g6)
    c: Coincident(g43,g5)
    c: Coincident(g43,g6)
    c: Coincident(g44,g7)
    c: Coincident(g44,g8)
    c: Coincident(g45,g7)
    c: Coincident(g45,g8)
    c: Distance(g30) = 256
    c: Distance(g33) = 100
FEATURE [Part::Extrusion] Extrude002
  Base = -> Sketch001
  Dir = (1,0,0)
  DirMode = 2
  FaceMakerClass = Part::FaceMakerBullseye
  LengthFwd = 8
  LengthRev = 0
  Solid = true
  Symmetric = false
FEATURE [Sketcher::SketchObject] Sketch002
  FullyConstrained = true
  sketch-geometry (20):
    g0: LineSegment StartX=-2.77179 StartY=-200.304 StartZ=0 EndX=5.22821 EndY=-200.304 EndZ=0
    g1: LineSegment StartX=5.22821 StartY=-200.304 StartZ=0 EndX=5.22821 EndY=-197.304 EndZ=0
    g2: LineSegment StartX=-2.77179 StartY=-200.304 StartZ=0 EndX=-2.77179 EndY=-197.304 EndZ=0
    g3: LineSegment StartX=5.22821 StartY=-197.304 StartZ=0 EndX=8.22821 EndY=-197.304 EndZ=0
    g4: LineSegment StartX=-2.77179 StartY=-197.304 StartZ=0 EndX=-5.77179 EndY=-197.304 EndZ=0
    g5: LineSegment StartX=19.2282 StartY=-203.304 StartZ=0 EndX=19.2282 EndY=-206.304 EndZ=0
    g6: LineSegment StartX=-16.7718 StartY=-203.304 StartZ=0 EndX=-16.7718 EndY=-206.304 EndZ=0
    g7: LineSegment StartX=-16.7718 StartY=-206.304 StartZ=0 EndX=19.2282 EndY=-206.304 EndZ=0
    g8: Circle CenterX=-16.7718 CenterY=-203.304 CenterZ=0 NormalX=0 NormalY=0 NormalZ=1 AngleXU=0 Radius=1
    g9: Circle CenterX=-5.77179 CenterY=-203.304 CenterZ=0 NormalX=0 NormalY=0 NormalZ=1 AngleXU=0 Radius=1
    g10: Circle CenterX=-5.77179 CenterY=-197.304 CenterZ=0 NormalX=0 NormalY=0 NormalZ=1 AngleXU=0 Radius=1
    g11: BSplineCurve PolesCount=3 KnotsCount=2 Degree=2 IsPeriodic=0
    g12: GeomPoint X=-16.7718 Y=-203.304 Z=0
    g13: GeomPoint X=-5.77179 Y=-197.304 Z=0
    g14: Circle CenterX=19.2282 CenterY=-203.304 CenterZ=0 NormalX=0 NormalY=0 NormalZ=1 AngleXU=0 Radius=1
    g15: Circle CenterX=8.22821 CenterY=-203.304 CenterZ=0 NormalX=0 NormalY=0 NormalZ=1 AngleXU=0 Radius=1
    g16: Circle CenterX=8.22821 CenterY=-197.304 CenterZ=0 NormalX=0 NormalY=0 NormalZ=1 AngleXU=0 Radius=1
    g17: BSplineCurve PolesCount=3 KnotsCount=2 Degree=2 IsPeriodic=0
    g18: GeomPoint X=19.2282 Y=-203.304 Z=0
    g19: GeomPoint X=8.22821 Y=-197.304 Z=0
  constraints (41):
    c: Horizontal(g0)
    c: Distance(g0) = 8
    c: Coincident(g1,g0)
    c: Vertical(g1)
    c: Distance(g1) = 3
    c: Coincident(g2,g0)
    c: Vertical(g2)
    c: Distance(g2) = 3
    c: Coincident(g3,g1)
    c: Horizontal(g3)
    c: Distance(g3) = 3
    c: Coincident(g4,g2)
    c: Horizontal(g4)
    c: Distance(g4) = 3
    c: Vertical(g5)
    c: Vertical(g6)
    c: Coincident(g7,g6)
    c: Coincident(g7,g5)
    c: Weight(g8) = 1
    c: Equal(g8,g9)
    c: Equal(g8,g10)
    c: Coincident(g11,g4)
    c: InternalAlignment(g8,g11)
    c: InternalAlignment(g9,g11)
    c: InternalAlignment(g10,g11)
    c: InternalAlignment(g12,g11)
    c: InternalAlignment(g13,g11)
    c: Coincident(g17,g5)
    c: Weight(g14) = 1
    c: Equal(g14,g15)
    c: Equal(g14,g16)
    c: Coincident(g17,g3)
    c: InternalAlignment(g14,g17)
    c: InternalAlignment(g15,g17)
    c: InternalAlignment(g16,g17)
    c: InternalAlignment(g18,g17)
    c: InternalAlignment(g19,g17)
    c: Block(g7)
    c: Block(g17)
    c: Block(g11)
    c: Block(g6)
FEATURE [Part::Extrusion] Extrude003
  Base = -> Sketch002
  Dir = (0,0,1)
  DirMode = 2
  FaceMakerClass = Part::FaceMakerBullseye
  LengthFwd = 260
  LengthRev = 0
  Solid = true
  Symmetric = false
FEATURE [Part::Extrusion] Extrude
  Base = -> Sketch
  Dir = (0,0,1)
  DirMode = 2
  FaceMakerClass = Part::FaceMakerBullseye
  LengthFwd = 14
  LengthRev = 0
  Solid = true
  Symmetric = false
